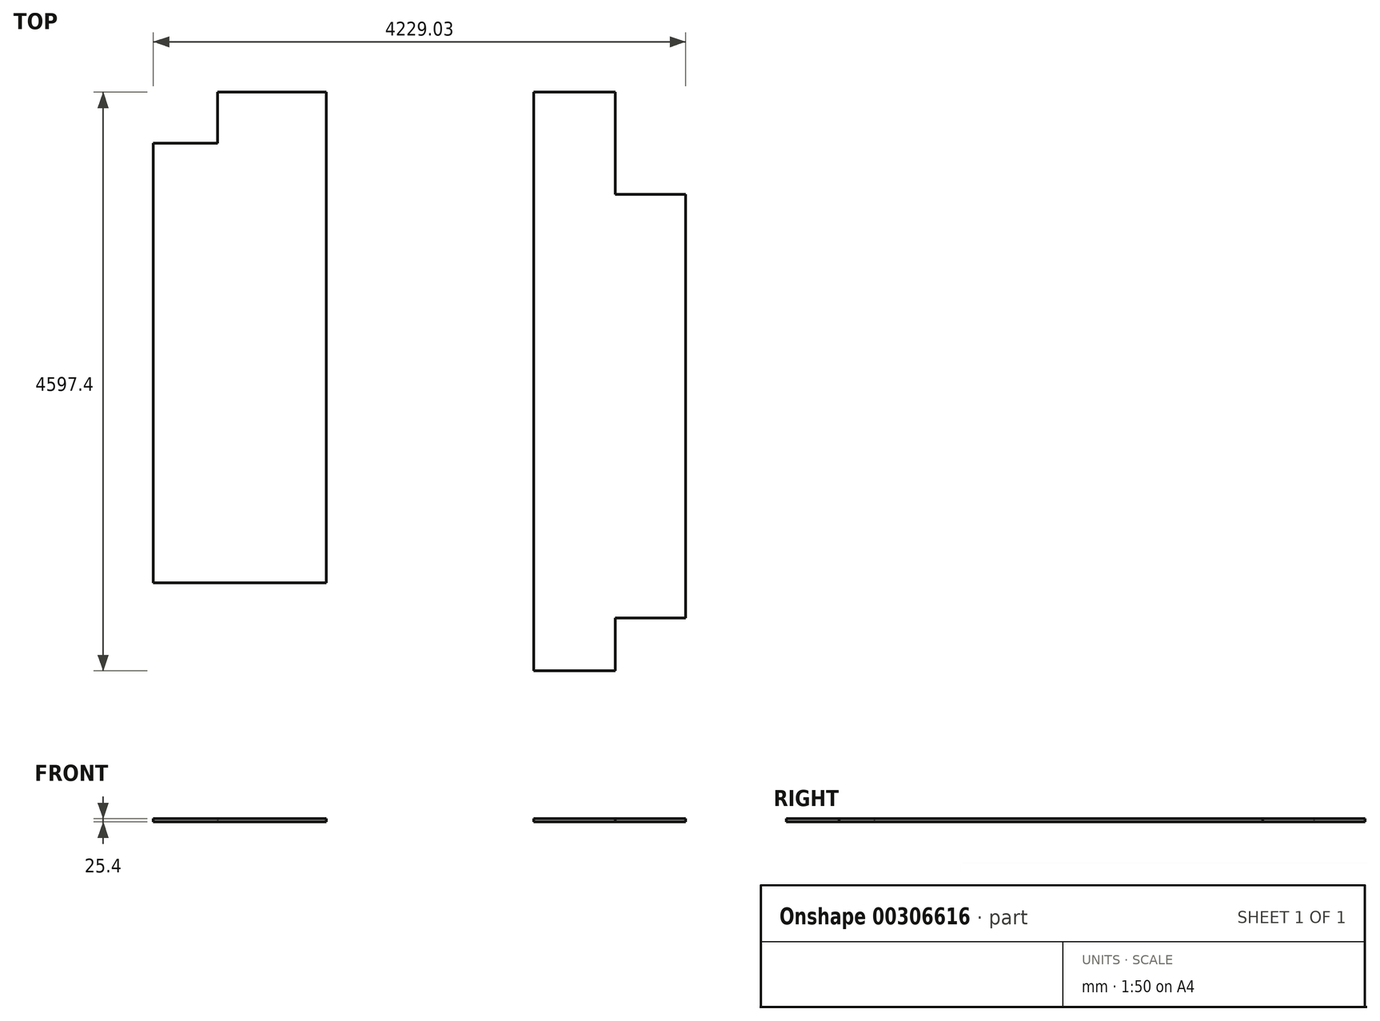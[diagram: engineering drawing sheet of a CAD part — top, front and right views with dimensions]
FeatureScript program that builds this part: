
annotation { "Feature Type Name" : "Feature", "Feature Type Description" : "" }
export const myFeature = defineFeature(function(context is Context, id is Id, definition is map)
    precondition{}
    {
        {
            var Q0;
            Q0=qCreatedBy(makeId("Top.planeOp"),FACE);
            var sketch = newSketch(context, id + "F0", { "sketchPlane" : qUnion([Q0])});
            skLineSegment(sketch, "E0.bottom", {"start": v(0, 0) * mm, "end": v(1371.6, 0) * mm});
            skLineSegment(sketch, "E0.top", {"start": v(508, 3898.9) * mm, "end": v(1371.6, 3898.9) * mm});
            skLineSegment(sketch, "E0.left", {"start": v(0, 0) * mm, "end": v(0, 3492.5) * mm});
            skLineSegment(sketch, "E0.right", {"start": v(1371.6, 0) * mm, "end": v(1371.6, 3898.9) * mm});
            skLineSegment(sketch, "E1", {"start": v(508, 3898.9) * mm, "end": v(508, 3492.5) * mm});
            skLineSegment(sketch, "E2", {"start": v(508, 3492.5) * mm, "end": v(0, 3492.5) * mm});
            skLineSegment(sketch, "E3.0", {"start": v(0, 1219.2) * mm, "end": v(1371.6, 1219.2) * mm});
            skLineSegment(sketch, "E4.0", {"start": v(0, 2438.4) * mm, "end": v(1371.6, 2438.4) * mm});
            skLineSegment(sketch, "E5.0", {"start": v(0, 3657.6) * mm, "end": v(1371.6, 3657.6) * mm});
            skSolve(sketch);
        }
        {
            var Q0;
            Q0 = qSketchRegion(id + "F0", true);
            extrude(context, id + "F1", {"entities" : qUnion([Q0]), "depth" : 25.4 * mm});
        }
        {
            var Q0;
            Q0=qCreatedBy(makeId("Top.planeOp"),FACE);
            var sketch = newSketch(context, id + "F2", { "sketchPlane" : qUnion([Q0])});
            skLineSegment(sketch, "E6.bottom", {"start": v(3022.53, 3898.9) * mm, "end": v(3670.23, 3898.9) * mm});
            skLineSegment(sketch, "E6.top", {"start": v(3022.53, -698.5) * mm, "end": v(3771.83, -698.5) * mm});
            skLineSegment(sketch, "E6.left", {"start": v(3022.53, 3898.9) * mm, "end": v(3022.53, -698.5) * mm});
            skLineSegment(sketch, "E6.right", {"start": v(4229.03, 3086.1) * mm, "end": v(4229.03, -279.4) * mm});
            skLineSegment(sketch, "E7.top", {"start": v(4229.03, 3086.1) * mm, "end": v(3670.23, 3086.1) * mm});
            skLineSegment(sketch, "E7.right", {"start": v(3670.23, 3898.9) * mm, "end": v(3670.23, 3086.1) * mm});
            skLineSegment(sketch, "E8", {"start": v(3670.23, 3086.1) * mm, "end": v(3670.23, -698.5) * mm, "construction": true});
            skLineSegment(sketch, "E9", {"start": v(3771.83, 3086.1) * mm, "end": v(3771.83, -698.5) * mm, "construction": true});
            skLineSegment(sketch, "E10", {"start": v(3670.23, -698.5) * mm, "end": v(3670.23, -279.4) * mm});
            skLineSegment(sketch, "E11", {"start": v(3670.23, -279.4) * mm, "end": v(4229.03, -279.4) * mm});
            skSolve(sketch);
        }
        {
            var Q0;
            Q0 = qSketchRegion(id + "F2", true);
            extrude(context, id + "F3", {"entities" : qUnion([Q0]), "depth" : 25.4 * mm});
        }
    });
